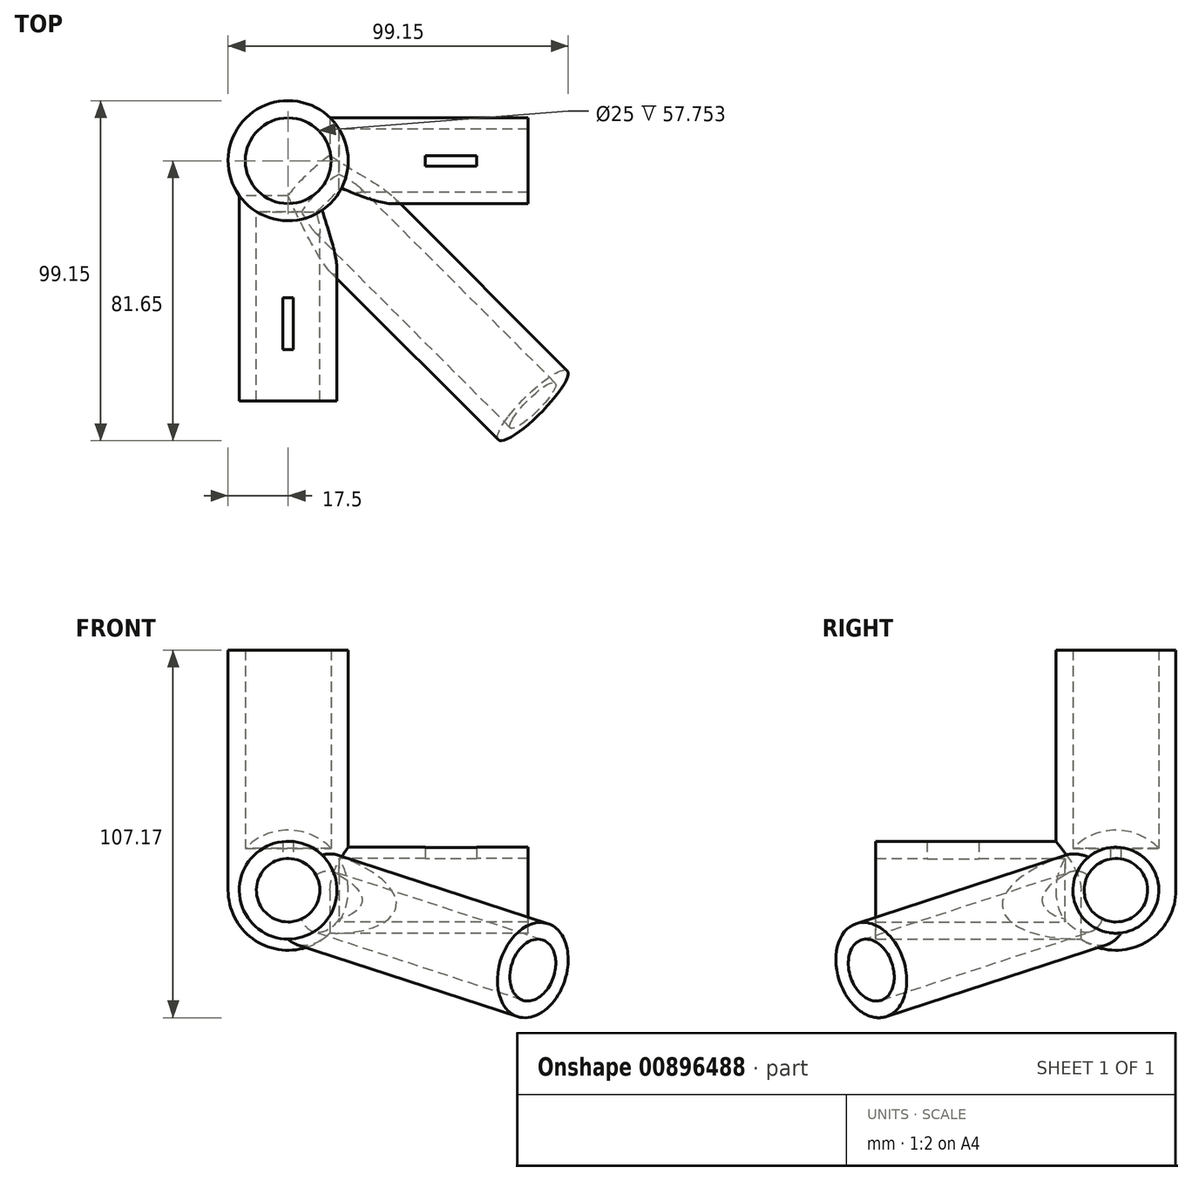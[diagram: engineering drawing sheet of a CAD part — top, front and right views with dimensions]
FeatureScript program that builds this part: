
annotation { "Feature Type Name" : "Feature", "Feature Type Description" : "" }
export const myFeature = defineFeature(function(context is Context, id is Id, definition is map)
    precondition{}
    {
        {
            assignVariable(context, id + "F0", {"name" : "mala_vnitrni_prumer", "anyValue" : 18.5 * mm});
        }
        {
            assignVariable(context, id + "F1", {"name" : "delka_trubky", "anyValue" : 70 * mm});
        }
        {
            assignVariable(context, id + "F2", {"name" : "sila_steny", "anyValue" : 5 * mm});
        }
        {
            assignVariable(context, id + "F3", {"name" : "zarazka_vyska", "anyValue" : 10 * mm});
        }
        {
            assignVariable(context, id + "F4", {"name" : "uhel", "anyValue" : 13});
        }
        {
            assignVariable(context, id + "F5", {"name" : "zarazka_tloustka", "anyValue" : 3 * mm});
        }
        {
            var Q0;
            Q0=qCreatedBy(makeId("Top.planeOp"),FACE);
            var sketch = newSketch(context, id + "F6", { "sketchPlane" : qUnion([Q0])});
            skCircle(sketch, "E0", {"center": v(0, 0) * mm, "radius": 12.5 * mm});
            skCircle(sketch, "E1.0", {"center": v(0, 0) * mm, "radius": 17.5 * mm});
            skLineSegment(sketch, "E2.bottom", {"start": v(55, 1.43) * mm, "end": v(40, 1.43) * mm});
            skLineSegment(sketch, "E2.top", {"start": v(55, -1.57) * mm, "end": v(40, -1.57) * mm});
            skLineSegment(sketch, "E2.left", {"start": v(55, 1.43) * mm, "end": v(55, -1.57) * mm});
            skLineSegment(sketch, "E2.right", {"start": v(40, 1.43) * mm, "end": v(40, -1.57) * mm});
            skLineSegment(sketch, "E3.1.0", {"start": v(1.5, -40) * mm, "end": v(-1.5, -40) * mm});
            skLineSegment(sketch, "E3.1.1", {"start": v(1.5, -55) * mm, "end": v(1.5, -40) * mm});
            skLineSegment(sketch, "E3.1.2", {"start": v(1.5, -55) * mm, "end": v(-1.5, -55) * mm});
            skLineSegment(sketch, "E3.1.3", {"start": v(-1.5, -55) * mm, "end": v(-1.5, -40) * mm});
            skLineSegment(sketch, "E3.anchor1", {"start": v(0, 0) * mm, "end": v(20, -1.5) * mm, "construction": true});
            skLineSegment(sketch, "E3.anchor2", {"start": v(0, 0) * mm, "end": v(-1.5, -20) * mm, "construction": true});
            skSolve(sketch);
        }
        {
            var Q0;
            Q0=makeQuery(id+"F6.imprint","IMPRINT",FACE,{"disambiguationData":[TD([[makeQuery(id+"F6.imprint","IMPRINT",EDGE,{"derivedFrom":sQuery(id+"F6.wireOp",EDGE,"894MJo6l-Esmm-qZQB-KpMg-LODTdIt9MWhA")}),1.0]])]});
            var Q1;
            Q1=makeQuery(id+"F6.imprint","IMPRINT",FACE,{"disambiguationData":[TD([[makeQuery(id+"F6.imprint","IMPRINT",EDGE,{"derivedFrom":sQuery(id+"F6.wireOp",EDGE,"E0")}),-1.0]])]});
            extrude(context, id + "F7", {"entities" : qUnion([Q0, Q1]), "depth" : getVariable(context, 'delka_trubky'), "offsetDistance" : 25 * mm});
        }
        {
            var Q0;
            Q0=qCreatedBy(makeId("Front.planeOp"),FACE);
            var sketch = newSketch(context, id + "F8", { "sketchPlane" : qUnion([Q0])});
            skCircle(sketch, "E4", {"center": v(0, 0) * mm, "radius": 9.25 * mm});
            skCircle(sketch, "E5.0", {"center": v(0, 0) * mm, "radius": 14.25 * mm});
            skSolve(sketch);
        }
        {
            var Q0;
            Q0=makeQuery(id+"F8.imprint","IMPRINT",FACE,{"disambiguationData":[TD([[makeQuery(id+"F8.imprint","IMPRINT",EDGE,{"derivedFrom":sQuery(id+"F8.wireOp",EDGE,"E4")}),-1.0]])]});
            extrude(context, id + "F9", {"entities" : qUnion([Q0]), "operationType" : NewBodyOperationType.ADD, "depth" : getVariable(context, 'delka_trubky'), "offsetDistance" : 25 * mm});
        }
        {
            var Q0;
            Q0=qCreatedBy(makeId("Right.planeOp"),FACE);
            var sketch = newSketch(context, id + "F10", { "sketchPlane" : qUnion([Q0])});
            skCircle(sketch, "E6", {"center": v(0, 0) * mm, "radius": 9.25 * mm});
            skCircle(sketch, "E7.0", {"center": v(0, 0) * mm, "radius": 12.53 * mm});
            skSolve(sketch);
        }
        {
            var Q0;
            Q0 = qSketchRegion(id + "F10", true);
            extrude(context, id + "F11", {"entities" : qUnion([Q0]), "operationType" : NewBodyOperationType.ADD, "depth" : getVariable(context, 'delka_trubky'), "offsetDistance" : 25 * mm});
        }
        {
            var Q0;
            Q0=qCreatedBy(makeId("Front.planeOp"),FACE);
            var Q1;
            Q1=qCreatedBy(makeId("Right.planeOp"),FACE);
            cPlane(context, id + "F12", {"entities" : qUnion([Q0, Q1]), "cplaneType" : CPlaneType.MID_PLANE, "offset" : 25 * mm, "flipAlignment" : true, "width" : 150 * mm, "height" : 150 * mm});
        }
        {
            var Q0;
            Q0=qCreatedBy(id+"F12.planeOp",FACE);
            var sketch = newSketch(context, id + "F13", { "sketchPlane" : qUnion([Q0])});
            skLineSegment(sketch, "E8", {"start": v(-50.85, 6.56) * mm, "end": v(47.2, 6.56) * mm});
            skSolve(sketch);
        }
        {
            var Q0;
            Q0 = qBodyType(qCreatedBy(id + "F13" ,EDGE), BodyType.WIRE);
            cPlane(context, id + "F14", {"entities" : qUnion([Q0]), "cplaneType" : CPlaneType.LINE_ANGLE, "offset" : 25 * mm, "angle" : (90 + getVariable(context, 'uhel')) * degree, "width" : 150 * mm, "height" : 150 * mm});
        }
        {
            var Q0;
            Q0=qCreatedBy(id+"F14.planeOp",FACE);
            var sketch = newSketch(context, id + "F15", { "sketchPlane" : qUnion([Q0])});
            skCircle(sketch, "E9", {"center": v(0, 0) * mm, "radius": 9.25 * mm});
            skCircle(sketch, "E10.0", {"center": v(0, 0) * mm, "radius": 14.25 * mm});
            skSolve(sketch);
        }
        {
            var Q0;
            Q0 = qSketchRegion(id + "F15", true);
            extrude(context, id + "F16", {"entities" : qUnion([Q0]), "operationType" : NewBodyOperationType.ADD, "depth" : getVariable(context, 'delka_trubky') * 1.5, "offsetDistance" : 25 * mm});
        }
        {
            var Q0;
            Q0=qCreatedBy(makeId("Top.planeOp"),FACE);
            var sketch = newSketch(context, id + "F17", { "sketchPlane" : qUnion([Q0])});
            skLineSegment(sketch, "E11", {"start": v(0, -17.5) * mm, "end": v(0, 17.5) * mm});
            skArc(sketch, "E12", {"start": v(0, -17.5) * mm, "mid": v(17.5, 0) * mm, "end": v(0, 17.5) * mm});
            skSolve(sketch);
        }
        {
            var Q0;
            Q0 = qSketchRegion(id + "F17", true);
            var Q1;
            Q1=sQuery(id+"F17.wireOp",EDGE,"E11");
            revolve(context, id + "F18", {"operationType" : NewBodyOperationType.REMOVE, "surfaceOperationType" : NewSurfaceOperationType.NEW, "entities" : qUnion([Q0]), "axis" : qUnion([Q1]), "revolveType" : RevolveType.FULL});
        }
        {
            var Q0;
            Q0=makeQuery(id+"F6.imprint","IMPRINT",FACE,{"disambiguationData":[TD([[makeQuery(id+"F6.imprint","IMPRINT",EDGE,{"derivedFrom":sQuery(id+"F6.wireOp",EDGE,"E0")}),1.0]])]});
            var Q1;
            Q1=sQuery(id+"F6.wireOp",EDGE,"E0");
            extrude(context, id + "F19", {"entities" : qUnion([Q0]), "operationType" : NewBodyOperationType.REMOVE, "surfaceOperationType" : NewSurfaceOperationType.ADD, "surfaceEntities" : qUnion([Q1]), "depth" : 50 * mm, "offsetDistance" : 25 * mm});
        }
        {
            var Q0;
            Q0=makeQuery(id+"F8.imprint","IMPRINT",FACE,{"disambiguationData":[TD([[makeQuery(id+"F8.imprint","IMPRINT",EDGE,{"derivedFrom":sQuery(id+"F8.wireOp",EDGE,"E4")}),1.0]])]});
            extrude(context, id + "F20", {"entities" : qUnion([Q0]), "operationType" : NewBodyOperationType.REMOVE, "depth" : 51 * mm, "offsetDistance" : 25 * mm});
        }
        {
            var Q0;
            Q0=makeQuery(id+"F15.imprint","IMPRINT",FACE,{"disambiguationData":[TD([[makeQuery(id+"F15.imprint","IMPRINT",EDGE,{"derivedFrom":sQuery(id+"F15.wireOp",EDGE,"E9")}),1.0]])]});
            extrude(context, id + "F21", {"entities" : qUnion([Q0]), "operationType" : NewBodyOperationType.REMOVE, "depth" : 50 * mm, "offsetDistance" : 25 * mm});
        }
        {
            var Q0;
            Q0=makeQuery(id+"F10.imprint","IMPRINT",FACE,{"disambiguationData":[TD([[makeQuery(id+"F10.imprint","IMPRINT",EDGE,{"derivedFrom":sQuery(id+"F10.wireOp",EDGE,"E6")}),1.0]])]});
            var Q1;
            Q1=sQuery(id+"F10.wireOp",EDGE,"E6");
            extrude(context, id + "F22", {"entities" : qUnion([Q0]), "operationType" : NewBodyOperationType.REMOVE, "surfaceEntities" : qUnion([Q1]), "depth" : 50 * mm, "offsetDistance" : 25 * mm});
        }
        {
            var Q0;
            Q0=makeQuery(id+"F17.imprint","IMPRINT",FACE,{"disambiguationData":[TD([[makeQuery(id+"F17.imprint","IMPRINT",EDGE,{"derivedFrom":sQuery(id+"F17.wireOp",EDGE,"E11")}),-1.0]])]});
            var Q1;
            Q1=sQuery(id+"F17.wireOp",EDGE,"E11");
            revolve(context, id + "F23", {"operationType" : NewBodyOperationType.ADD, "surfaceOperationType" : NewSurfaceOperationType.NEW, "entities" : qUnion([Q0]), "axis" : qUnion([Q1]), "revolveType" : RevolveType.FULL});
        }
        {
            var Q0;
            Q0=qCreatedBy(makeId("Top.planeOp"),FACE);
            cPlane(context, id + "F24", {"entities" : qUnion([Q0]), "cplaneType" : CPlaneType.OFFSET, "offset" : getVariable(context, 'zarazka_vyska'), "width" : 150 * mm, "height" : 150 * mm});
        }
        {
            var Q0;
            Q0=qCreatedBy(id+"F24.planeOp",FACE);
            var sketch = newSketch(context, id + "F25", { "sketchPlane" : qUnion([Q0])});
            skCircle(sketch, "E13", {"center": v(0, 0) * mm, "radius": 12.5 * mm});
            skCircle(sketch, "E14.0", {"center": v(0, 0) * mm, "radius": 9.5 * mm});
            skSolve(sketch);
        }
        {
            var Q0;
            Q0=makeQuery(id+"F25.imprint","IMPRINT",FACE,{"disambiguationData":[TD([[makeQuery(id+"F25.imprint","IMPRINT",EDGE,{"derivedFrom":sQuery(id+"F25.wireOp",EDGE,"E13")}),1.0]])]});
            extrude(context, id + "F26", {"entities" : qUnion([Q0]), "operationType" : NewBodyOperationType.ADD, "oppositeDirection" : true, "depth" : getVariable(context, 'zarazka_tloustka'), "offsetDistance" : 25 * mm});
        }
        {
            var Q0;
            Q0=makeQuery(id+"F6.imprint","IMPRINT",FACE,{"disambiguationData":[TD([[makeQuery(id+"F6.imprint","IMPRINT",EDGE,{"derivedFrom":sQuery(id+"F6.wireOp",EDGE,"E2.bottom")}),1.0]])]});
            var Q1;
            Q1=sQuery(id+"F6.wireOp",EDGE,"E2.bottom");
            var Q2;
            Q2=sQuery(id+"F6.wireOp",EDGE,"E2.right");
            var Q3;
            Q3=sQuery(id+"F6.wireOp",EDGE,"E2.left");
            var Q4;
            Q4=sQuery(id+"F6.wireOp",EDGE,"E2.top");
            extrude(context, id + "F27", {"entities" : qUnion([Q0]), "operationType" : NewBodyOperationType.REMOVE, "surfaceEntities" : qUnion([Q1, Q2, Q3, Q4]), "depth" : getVariable(context, 'mala_vnitrni_prumer') + getVariable(context, 'sila_steny'), "offsetDistance" : 25 * mm});
        }
        {
            var Q0;
            Q0=makeQuery(id+"F6.imprint","IMPRINT",FACE,{"disambiguationData":[TD([[makeQuery(id+"F6.imprint","IMPRINT",EDGE,{"derivedFrom":sQuery(id+"F6.wireOp",EDGE,"E3.1.0")}),1.0]])]});
            extrude(context, id + "F28", {"entities" : qUnion([Q0]), "operationType" : NewBodyOperationType.REMOVE, "depth" : getVariable(context, 'mala_vnitrni_prumer') + getVariable(context, 'sila_steny'), "offsetDistance" : 25 * mm});
        }
        {
            var Q0;
            Q0=sQuery(id+"F13.wireOp",EDGE,"E8");
            cPlane(context, id + "F29", {"entities" : qUnion([Q0]), "cplaneType" : CPlaneType.LINE_ANGLE, "offset" : 25 * mm, "angle" : (getVariable(context, 'uhel')) * degree, "width" : 150 * mm, "height" : 150 * mm});
        }
    });
